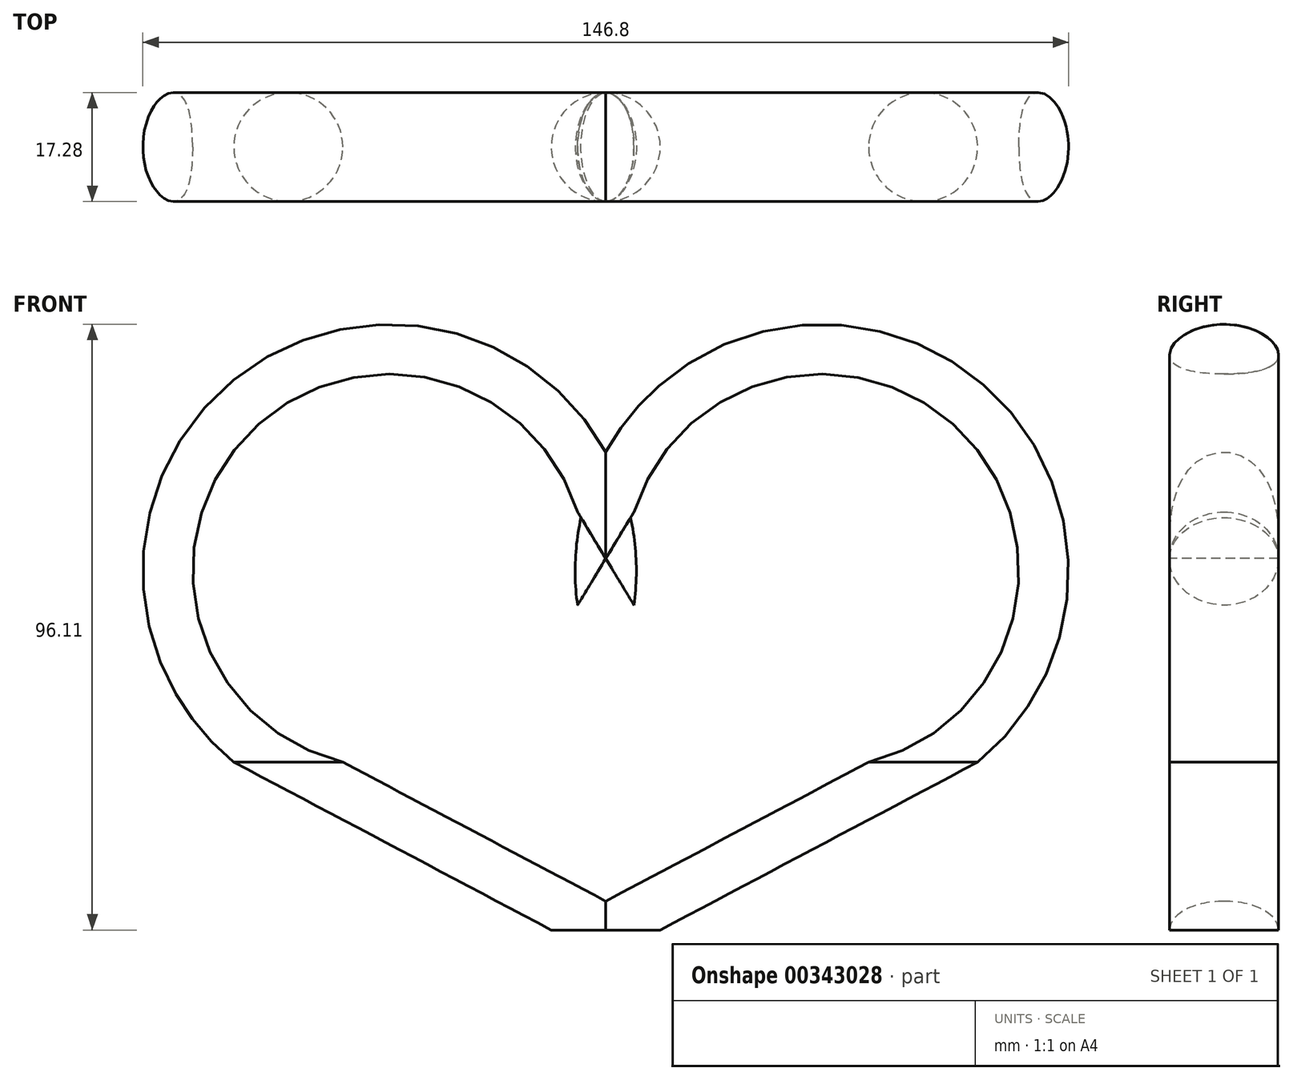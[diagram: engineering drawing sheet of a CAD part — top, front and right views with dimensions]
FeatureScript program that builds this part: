
annotation { "Feature Type Name" : "Feature", "Feature Type Description" : "" }
export const myFeature = defineFeature(function(context is Context, id is Id, definition is map)
    precondition{}
    {
        {
            var Q0;
            Q0=qCreatedBy(makeId("Front.planeOp"),FACE);
            var sketch = newSketch(context, id + "F0", { "sketchPlane" : qUnion([Q0])});
            skPoint(sketch, "E0.43.internal.orphan", {"position": v(-48.84, 0) * mm});
            skPoint(sketch, "E0.64.internal.orphan", {"position": v(0, -89.75) * mm});
            skPoint(sketch, "E0.74.internal.orphan", {"position": v(0, -22.9) * mm});
            skPoint(sketch, "E0.78.internal.orphan", {"position": v(-29.92, 0) * mm});
            skPoint(sketch, "E0.8.internal.orphan", {"position": v(57.08, 0) * mm});
            skLineSegment(sketch, "E1", {"start": v(0, 0) * mm, "end": v(-50.33, 26.64) * mm});
            skPoint(sketch, "E2.start.orphan", {"position": v(0, 77.83) * mm});
            skArc(sketch, "E3", {"start": v(0, 58.94) * mm, "mid": v(-52.81, 85.87) * mm, "end": v(-50.33, 26.64) * mm});
            skSolve(sketch);
        }
        {
            var Q0;
            Q0=qCreatedBy(makeId("Top.planeOp"),FACE);
            var sketch = newSketch(context, id + "F1", { "sketchPlane" : qUnion([Q0])});
            skCircle(sketch, "E4", {"center": v(0, 0) * mm, "radius": 8.64 * mm});
            skSolve(sketch);
        }
        {
            var Q0;
            Q0=makeQuery(id+"F1.imprint","IMPRINT",FACE,{"disambiguationData":[TD([[makeQuery(id+"F1.imprint","IMPRINT",EDGE,{"derivedFrom":sQuery(id+"F1.wireOp",EDGE,"E4")}),1.0]])]});
            var Q1;
            Q1 = qConstructionFilter(qBodyType(qCreatedBy(id + "F0" ,EDGE), BodyType.WIRE), ConstructionObject.NO);
            sweep(context, id + "F2", {"profiles" : qUnion([Q0]), "path" : qUnion([Q1])});
        }
        {
            var Q0;
            Q0=makeQuery(id+"F2.opSweep","SWEPT_BODY",BODY,{"disambiguationData":[OSD([sQuery(id+"F0.wireOp",EDGE,"E2"),sQuery(id+"F1.wireOp",EDGE,"E4")])]});
            var Q1;
            Q1=qCreatedBy(makeId("Right.planeOp"),FACE);
            mirror(context, id + "F3", {"operationType" : NewBodyOperationType.ADD, "entities" : qUnion([Q0]), "mirrorPlane" : qUnion([Q1])});
        }
    });
